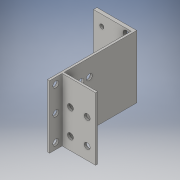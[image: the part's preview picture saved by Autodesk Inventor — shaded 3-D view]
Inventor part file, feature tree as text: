
AUTODESK INVENTOR PART (.ipt)
format: ipt  version: 2016 (Build 200138000, 138)  size: 188,416 bytes
history: native  units: mm
features: sketch x8, hole x5, extrude x3
ambient origin geometry x8: Origin, YZ Plane, XZ Plane, XY Plane, X Axis, Y Axis, Z Axis, Center Point
bodies: Body1 (feature_tree)
feature tree (16):
  extrude  "Extrusion2"  Depth=45.0mm
  extrude  "Extrusion3"  Depth=1.5mm
  hole  "Hole2"  [1 undecoded]
  hole  "Hole3"  [1 undecoded]
  hole  "Hole4"  [1 undecoded]
  extrude  "Extrusion4"  Depth=4.6mm
  hole  "Hole6"  [1 undecoded]
  hole  "Hole7"  [1 undecoded]
  sketch  "Sketch3"  dims[d27=27.0mm d28=45.0mm]
  sketch  "Sketch4"  dims[d29=2.5mm d30=0.0mm d31=1.5mm]
  sketch  "Sketch5"  dims[d32=45.0mm d33=60.0mm d34=2.5mm d35=0.0mm d36=0.0mm]
  sketch  "Sketch6"  dims[d45=4.6mm d46=3.5mm]
  sketch  "Sketch7"  dims[d47=3.5mm d50=4.6mm]
  sketch  "Sketch8"  dims[d51=3.5mm d52=4.6mm]
  sketch  "Sketch10"  dims[d53=4.6mm d54=6.0mm d55=4.0mm d56=2.0mm d57=90.0deg d58=8.0mm d59=0.0mm d61=3.5mm]
  sketch  "Sketch11"  dims[d62=3.5mm d63=3.5mm d64=3.0mm d65=6.0mm d66=7.5mm d67=3.0mm d68=18.0mm d69=3.0mm d70=6.0mm d71=4.0mm d72=2.0mm d73=90.0deg d74=8.0mm d75=0.0mm d76=4.3mm d77=4.5mm d78=4.5mm d79=4.3mm d80=4.5mm d81=4.5mm d82=4.3mm d83=4.3mm d84=6.0mm d85=4.0mm d86=2.0mm d87=90.0deg d88=8.0mm d89=0.0mm d90=45.0mm d91=1.5mm d92=52.0mm d93=24.0mm d94=0.0mm d95=4.25mm d96=9.0mm d97=6.0mm d100=4.25mm d102=9.0mm d110=4.25mm d111=6.0mm d112=4.0mm d113=2.0mm d114=90.0deg d115=8.0mm d116=20.594885mm d117=4.25mm d119=12.0mm d120=6.0mm d121=4.25mm d122=6.0mm d123=4.25mm d124=6.0mm d125=4.25mm d126=6.0mm d127=4.0mm d128=2.0mm d129=90.0deg d130=8.0mm d131=20.594885mm]
note: 5 required parameter values undecoded (feature->parameter linkage not recoverable at this tier; creation-order binding heuristic only, values carry confidence <= 0.55)
